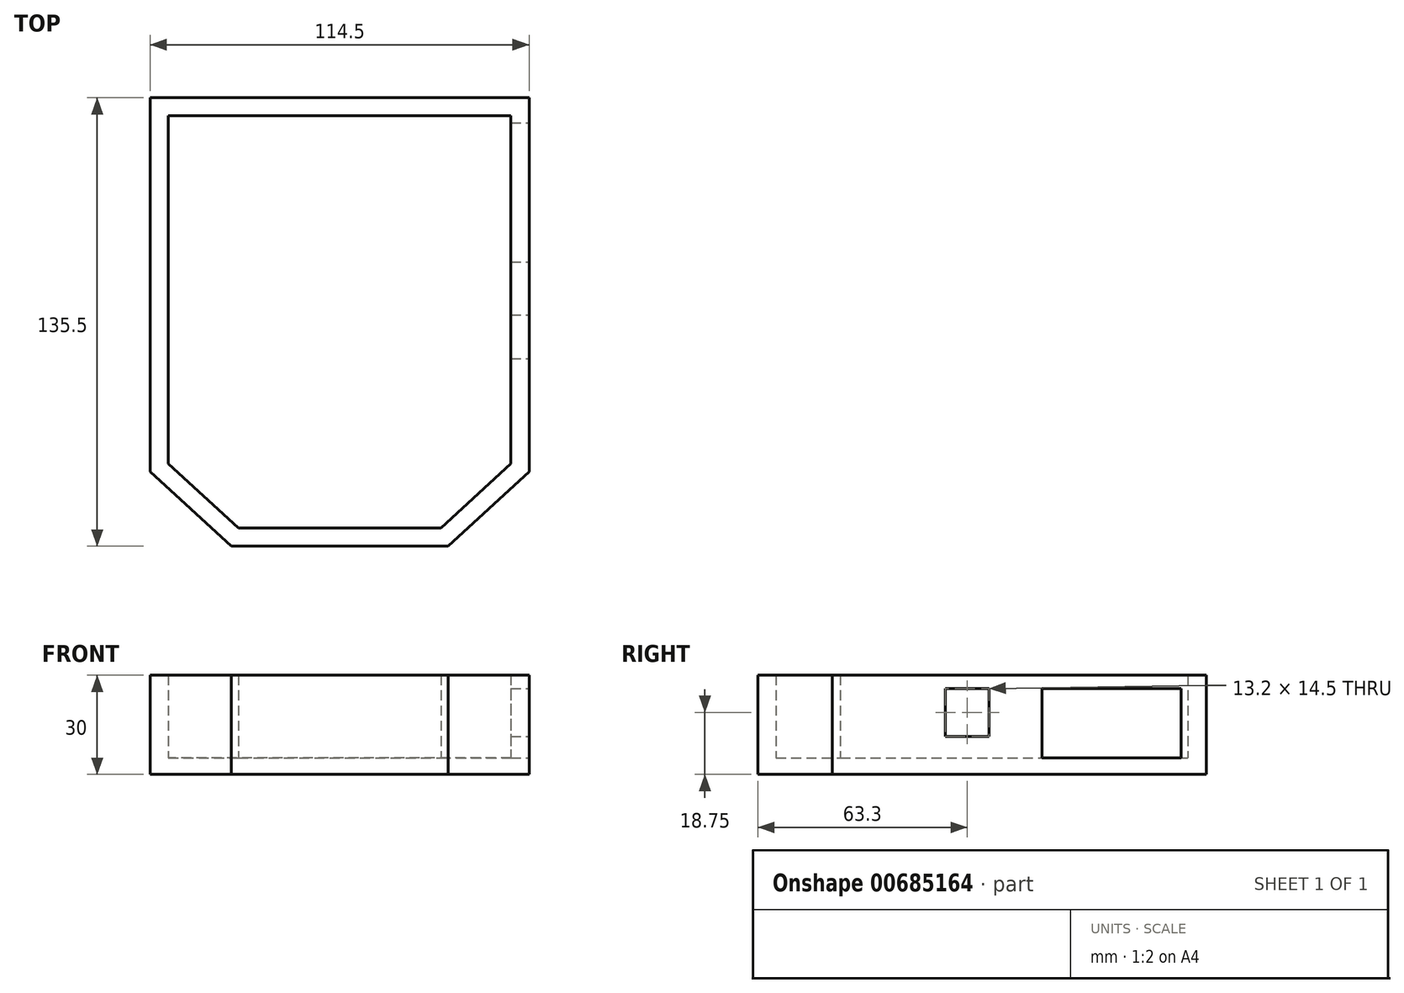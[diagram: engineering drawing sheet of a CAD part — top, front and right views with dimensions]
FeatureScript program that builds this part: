
annotation { "Feature Type Name" : "Feature", "Feature Type Description" : "" }
export const myFeature = defineFeature(function(context is Context, id is Id, definition is map)
    precondition{}
    {
        {
            var Q0;
            Q0=qCreatedBy(makeId("Top.planeOp"),FACE);
            var sketch = newSketch(context, id + "F0", { "sketchPlane" : qUnion([Q0])});
            skLineSegment(sketch, "E0.bottom", {"start": v(-24.5, 0) * mm, "end": v(-90, 0) * mm});
            skLineSegment(sketch, "E0.top", {"start": v(0, 135.5) * mm, "end": v(-114.5, 135.5) * mm});
            skLineSegment(sketch, "E0.left", {"start": v(0, 22.5) * mm, "end": v(0, 135.5) * mm});
            skLineSegment(sketch, "E0.right", {"start": v(-114.5, 22.5) * mm, "end": v(-114.5, 135.5) * mm});
            skLineSegment(sketch, "E1", {"start": v(-114.5, 22.5) * mm, "end": v(-90, 0) * mm});
            skLineSegment(sketch, "E2", {"start": v(-24.5, 0) * mm, "end": v(0, 22.5) * mm});
            skPoint(sketch, "E3.orphan", {"position": v(-114.5, 0) * mm});
            skPoint(sketch, "E4.orphan", {"position": v(0, 0) * mm});
            skSolve(sketch);
        }
        {
            var Q0;
            Q0 = qSketchRegion(id + "F0", true);
            extrude(context, id + "F1", {"entities" : qUnion([Q0]), "depth" : 5 * mm, "offsetDistance" : 25 * mm});
        }
        {
            var Q0;
            Q0=makeQuery(id+"F1.opExtrude","CAP_FACE",FACE,{"disambiguationData":[OSD([sQuery(id+"F0.wireOp",EDGE,"E0.bottom"),sQuery(id+"F0.wireOp",EDGE,"E0.top"),sQuery(id+"F0.wireOp",EDGE,"E0.left"),sQuery(id+"F0.wireOp",EDGE,"E0.right"),sQuery(id+"F0.wireOp",EDGE,"E1"),sQuery(id+"F0.wireOp",EDGE,"E2")])],"isStart":false});
            var sketch = newSketch(context, id + "F2", { "sketchPlane" : qUnion([Q0])});
            skLineSegment(sketch, "E5.0", {"start": v(-26.64, 5.5) * mm, "end": v(-5.5, 24.92) * mm});
            skLineSegment(sketch, "E5.1", {"start": v(-5.5, 130) * mm, "end": v(-109, 130) * mm});
            skLineSegment(sketch, "E5.2", {"start": v(-109, 130) * mm, "end": v(-109, 24.92) * mm});
            skLineSegment(sketch, "E5.3", {"start": v(-5.5, 24.92) * mm, "end": v(-5.5, 130) * mm});
            skLineSegment(sketch, "E5.4", {"start": v(-109, 24.92) * mm, "end": v(-87.86, 5.5) * mm});
            skLineSegment(sketch, "E5.5", {"start": v(-87.86, 5.5) * mm, "end": v(-26.64, 5.5) * mm});
            skSolve(sketch);
        }
        {
            var Q0;
            Q0=makeQuery(id+"F2.imprint","IMPRINT",FACE,{"disambiguationData":[TD([[makeQuery(id+"F2.imprint","IMPRINT",EDGE,{"derivedFrom":sQuery(id+"F2.wireOp",EDGE,"E5.0")}),-1.0]])]});
            extrude(context, id + "F3", {"entities" : qUnion([Q0]), "operationType" : NewBodyOperationType.ADD, "depth" : 25 * mm, "offsetDistance" : 25 * mm});
        }
        {
            var Q0;
            {var subQ0=sQuery(id+"F0.wireOp",EDGE,"E0.left");Q0=makeQuery(id+"F3.boolean.opBoolean","MERGE",FACE,{"derivedFrom":[makeQuery(id+"F1.opExtrude","SWEPT_FACE",FACE,{"disambiguationData":[OSD([subQ0])]}),makeQuery(id+"F3.opExtrude","SWEPT_FACE",FACE,{"disambiguationData":[OSD([subQ0])]})]});}
            var sketch = newSketch(context, id + "F4", { "sketchPlane" : qUnion([Q0])});
            skLineSegment(sketch, "E6.bottom", {"start": v(85.9, 26) * mm, "end": v(127.9, 26) * mm});
            skLineSegment(sketch, "E6.top", {"start": v(85.9, 5) * mm, "end": v(127.9, 5) * mm});
            skLineSegment(sketch, "E6.left", {"start": v(85.9, 26) * mm, "end": v(85.9, 5) * mm});
            skLineSegment(sketch, "E6.right", {"start": v(127.9, 26) * mm, "end": v(127.9, 5) * mm});
            skLineSegment(sketch, "E7.bottom", {"start": v(56.7, 26) * mm, "end": v(69.9, 26) * mm});
            skLineSegment(sketch, "E7.top", {"start": v(56.7, 11.5) * mm, "end": v(69.9, 11.5) * mm});
            skLineSegment(sketch, "E7.left", {"start": v(56.7, 26) * mm, "end": v(56.7, 11.5) * mm});
            skLineSegment(sketch, "E7.right", {"start": v(69.9, 26) * mm, "end": v(69.9, 11.5) * mm});
            skSolve(sketch);
        }
        {
            var Q0;
            Q0 = qSketchRegion(id + "F4", true);
            extrude(context, id + "F5", {"entities" : qUnion([Q0]), "operationType" : NewBodyOperationType.REMOVE, "endBound" : BoundingType.UP_TO_NEXT, "oppositeDirection" : true, "depth" : 25 * mm, "offsetDistance" : 25 * mm});
        }
    });
